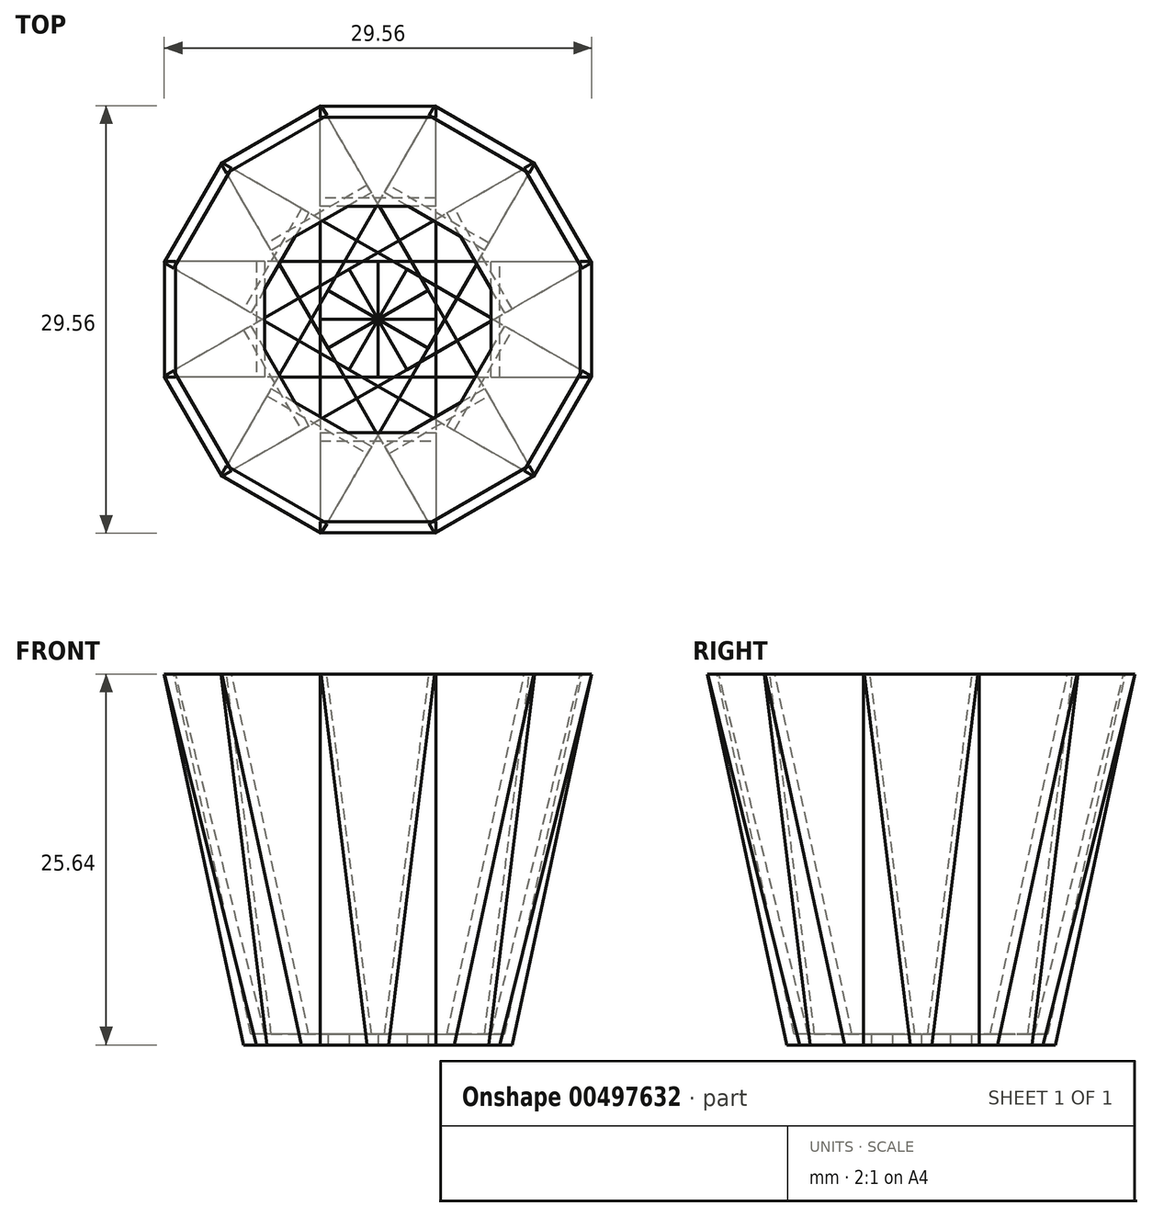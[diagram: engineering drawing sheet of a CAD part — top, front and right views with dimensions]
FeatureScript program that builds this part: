
annotation { "Feature Type Name" : "Feature", "Feature Type Description" : "" }
export const myFeature = defineFeature(function(context is Context, id is Id, definition is map)
    precondition{}
    {
        {
            var Q0;
            Q0=qCreatedBy(makeId("Front.planeOp"),FACE);
            var sketch = newSketch(context, id + "F0", { "sketchPlane" : qUnion([Q0])});
            skLineSegment(sketch, "E0", {"start": v(0, 0) * mm, "end": v(8.4, 0) * mm});
            skLineSegment(sketch, "E1", {"start": v(8.4, 0) * mm, "end": v(17.73, 24.89) * mm});
            skLineSegment(sketch, "E2.2", {"start": v(0, 2.1) * mm, "end": v(6.95, 2.1) * mm});
            skLineSegment(sketch, "E3", {"start": v(0, 2.1) * mm, "end": v(0, 0) * mm});
            skLineSegment(sketch, "E4", {"start": v(8.4, 0) * mm, "end": v(14.76, 25.64) * mm});
            skLineSegment(sketch, "E5.0", {"start": v(7.82, 0.75) * mm, "end": v(13.99, 25.64) * mm});
            skLineSegment(sketch, "E6.0", {"start": v(0, 0.75) * mm, "end": v(7.82, 0.75) * mm});
            skLineSegment(sketch, "E7", {"start": v(14.76, 25.64) * mm, "end": v(13.53, 25.64) * mm});
            skLineSegment(sketch, "E8.0", {"start": v(7.56, 0.75) * mm, "end": v(13.75, 25.7) * mm});
            skLineSegment(sketch, "E9.0", {"start": v(7.36, 0.75) * mm, "end": v(13.55, 25.75) * mm});
            skSolve(sketch);
        }
        {
            var Q0;
            Q0=makeQuery(id+"F0.imprint","IMPRINT",FACE,{"disambiguationData":[TD([[makeQuery(id+"F0.imprint","IMPRINT",EDGE,{"derivedFrom":sQuery(id+"F0.wireOp",EDGE,"E0")}),1.0]])]});
            extrude(context, id + "F1", {"entities" : qUnion([Q0]), "depth" : 4 * mm, "hasSecondDirection" : true, "secondDirectionOppositeDirection" : true, "secondDirectionDepth" : 4 * mm});
        }
        {
            var Q0;
            Q0=makeQuery(id+"F1.opExtrude","SWEPT_BODY",BODY,{"disambiguationData":[OSD([sQuery(id+"F0.wireOp",EDGE,"E0"),sQuery(id+"F0.wireOp",EDGE,"E1"),sQuery(id+"F0.wireOp",EDGE,"xv8VgBhu-qazy-YgqB-v8JE-5yVdrMK1Qche"),sQuery(id+"F0.wireOp",EDGE,"E2.0"),sQuery(id+"F0.wireOp",EDGE,"E2.1"),sQuery(id+"F0.wireOp",EDGE,"E2.2"),sQuery(id+"F0.wireOp",EDGE,"8E1QmZ2g-YMvP-tSYN-84yT-wLBnS1EG7rmy"),sQuery(id+"F0.wireOp",EDGE,"E3")])]});
            var Q1;
            Q1=sQuery(id+"F0.wireOp",EDGE,"E3");
            circularPattern(context, id + "F2", {"entities" : qUnion([Q0]), "axis" : qUnion([Q1]), "angle" : 360 * degree, "instanceCount" : 12, "equalSpace" : true});
        }
    });
